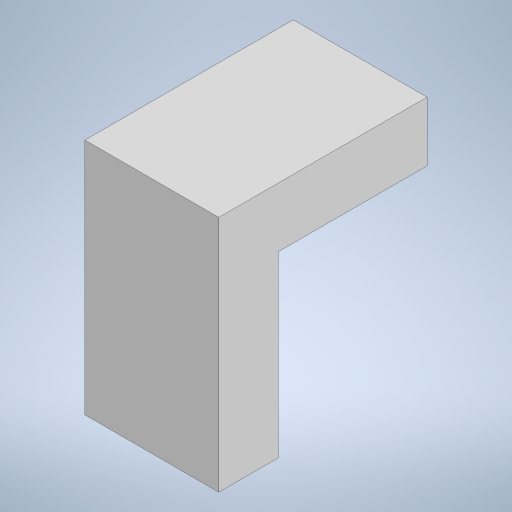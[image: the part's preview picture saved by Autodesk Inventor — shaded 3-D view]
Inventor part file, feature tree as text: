
AUTODESK INVENTOR PART (.ipt)
format: ipt  version: 2023.5 (Build 275446000, 446)  size: 192,000 bytes
history: native  units: mm
features: other x1, extrude x1, sketch x1
ambient origin geometry x8: Origin, YZ Plane, XZ Plane, XY Plane, X Axis, Y Axis, Z Axis, Center Point
bodies: Body1 (feature_tree)
feature tree (3):
  other  "Bryła1"
  extrude  "Wyciągnięcie proste1"  Depth=12.0mm
  sketch  "Szkic1"
